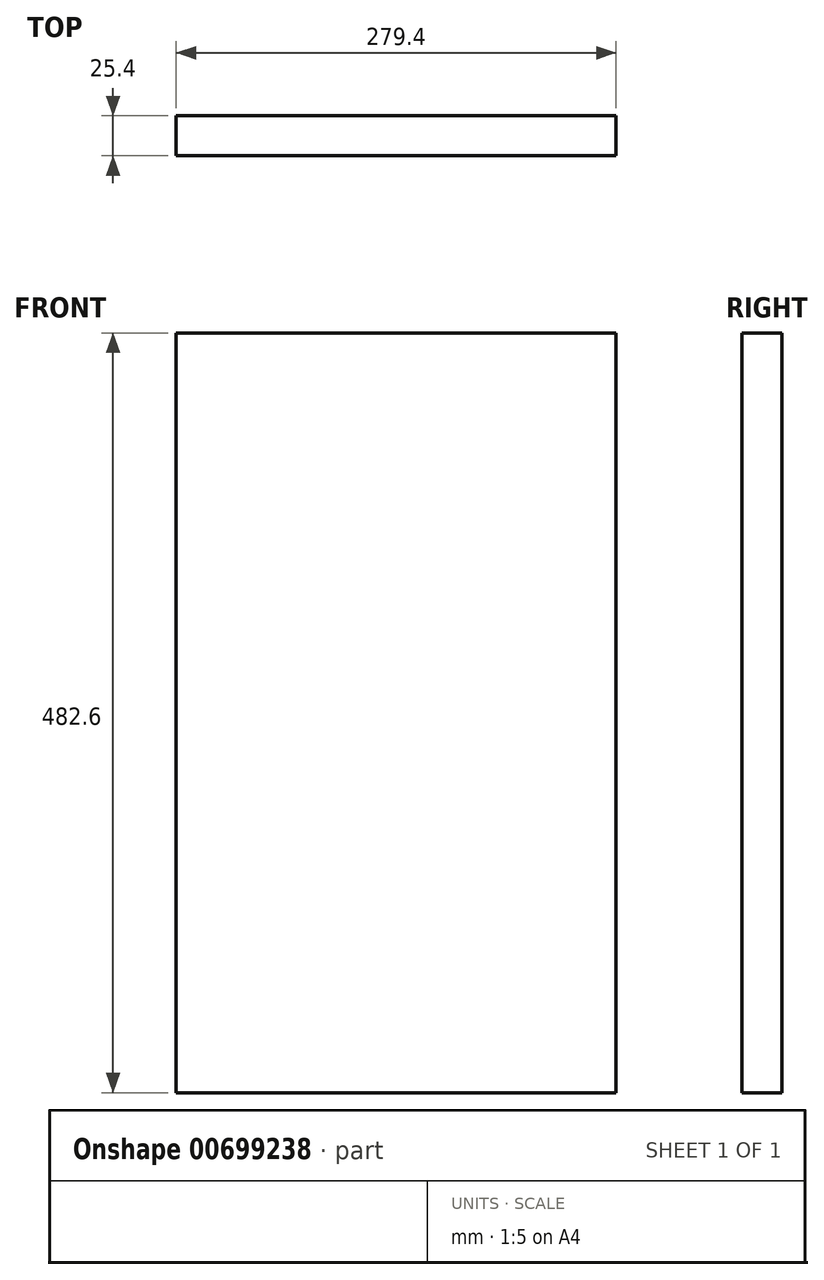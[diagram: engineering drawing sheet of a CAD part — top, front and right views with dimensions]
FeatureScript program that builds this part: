
annotation { "Feature Type Name" : "Feature", "Feature Type Description" : "" }
export const myFeature = defineFeature(function(context is Context, id is Id, definition is map)
    precondition{}
    {
        {
            var Q0;
            Q0=qCreatedBy(makeId("Front.planeOp"),FACE);
            var sketch = newSketch(context, id + "F0", { "sketchPlane" : qUnion([Q0])});
            skLineSegment(sketch, "E0.bottom", {"start": v(-25.6, -75.4) * mm, "end": v(253.8, -75.4) * mm});
            skLineSegment(sketch, "E0.top", {"start": v(-25.6, 407.2) * mm, "end": v(253.8, 407.2) * mm});
            skLineSegment(sketch, "E0.left", {"start": v(-25.6, -75.4) * mm, "end": v(-25.6, 407.2) * mm});
            skLineSegment(sketch, "E0.right", {"start": v(253.8, -75.4) * mm, "end": v(253.8, 407.2) * mm});
            skSolve(sketch);
        }
        {
            var Q0;
            Q0=makeQuery(id+"F0.imprint","IMPRINT",FACE,{"disambiguationData":[TD([[makeQuery(id+"F0.imprint","IMPRINT",EDGE,{"derivedFrom":sQuery(id+"F0.wireOp",EDGE,"E0.bottom")}),1.0]])]});
            extrude(context, id + "F1", {"entities" : qUnion([Q0]), "depth" : 25.4 * mm, "offsetDistance" : 25.4 * mm});
        }
    });
